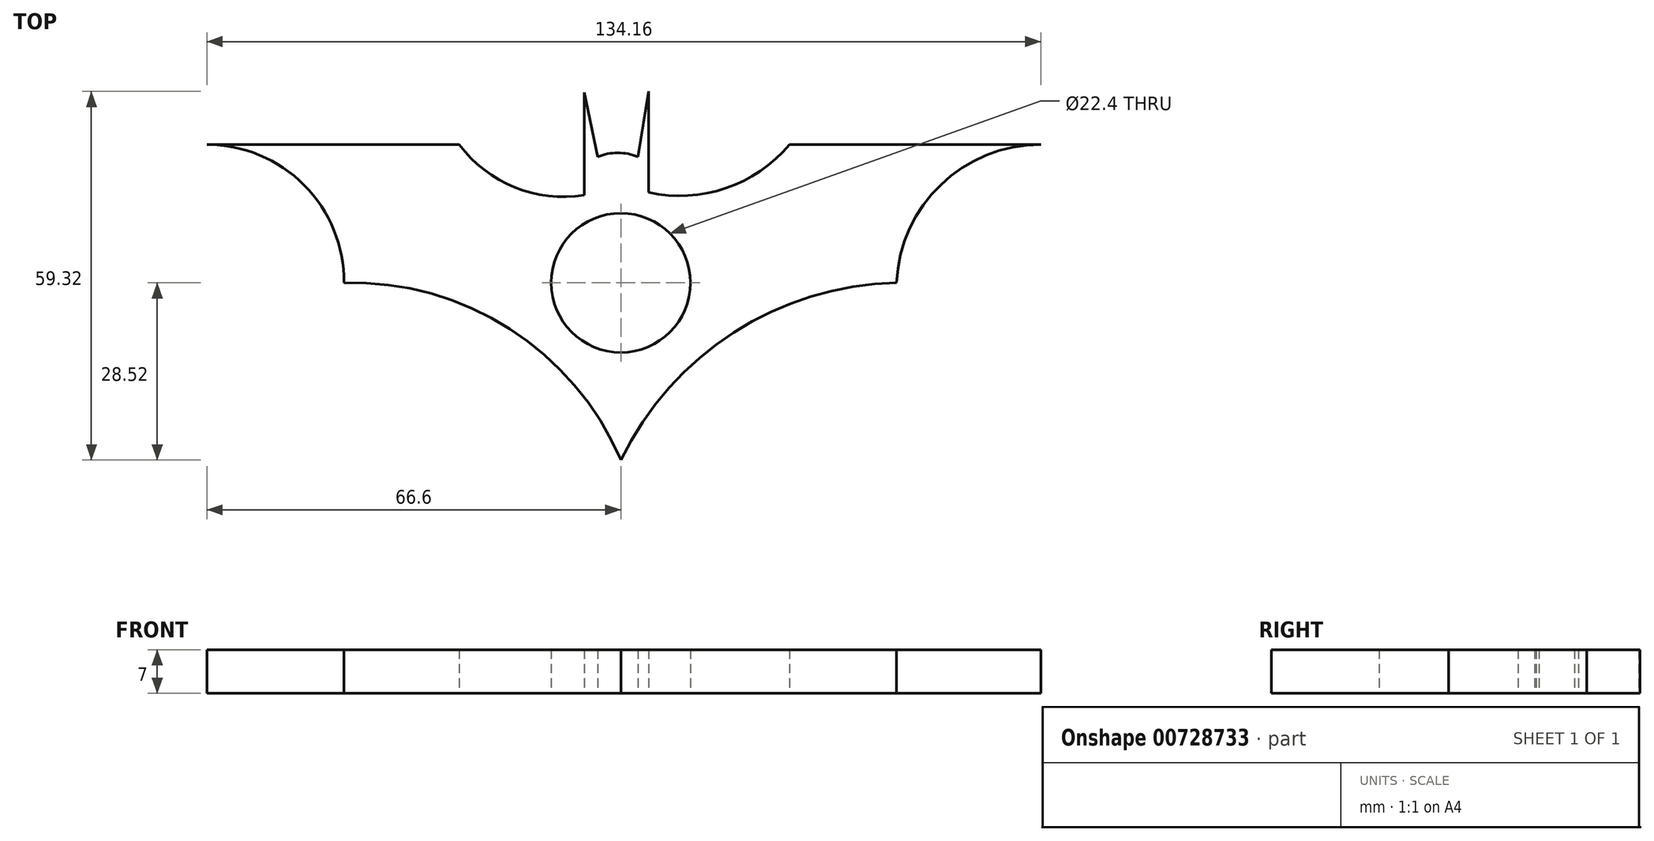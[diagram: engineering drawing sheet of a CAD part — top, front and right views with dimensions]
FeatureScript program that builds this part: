
annotation { "Feature Type Name" : "Feature", "Feature Type Description" : "" }
export const myFeature = defineFeature(function(context is Context, id is Id, definition is map)
    precondition{}
    {
        {
            var Q0;
            Q0=qCreatedBy(makeId("Top.planeOp"),FACE);
            var sketch = newSketch(context, id + "F0", { "sketchPlane" : qUnion([Q0])});
            skLineSegment(sketch, "E0", {"start": v(-66.6, 22.24) * mm, "end": v(-25.99, 22.24) * mm});
            skArc(sketch, "E1", {"start": v(67.56, 22.24) * mm, "mid": v(51.5, 15.78) * mm, "end": v(44.37, 0) * mm});
            skArc(sketch, "E2", {"start": v(-44.55, 0) * mm, "mid": v(-50.94, 15.72) * mm, "end": v(-66.6, 22.24) * mm});
            skArc(sketch, "E3", {"start": v(0, -28.52) * mm, "mid": v(-17.88, -7.4) * mm, "end": v(-44.55, 0) * mm});
            skArc(sketch, "E4", {"start": v(-25.99, 22.24) * mm, "mid": v(-17.09, 15.36) * mm, "end": v(-5.9, 14.12) * mm});
            skLineSegment(sketch, "E5", {"start": v(-5.9, 14.12) * mm, "end": v(-5.9, 30.6) * mm});
            skLineSegment(sketch, "E6", {"start": v(-5.9, 30.6) * mm, "end": v(-3.75, 20.26) * mm});
            skArc(sketch, "E7", {"start": v(2.77, 20.26) * mm, "mid": v(-0.5, 20.9) * mm, "end": v(-3.75, 20.26) * mm});
            skLineSegment(sketch, "E8", {"start": v(2.77, 20.26) * mm, "end": v(4.48, 30.8) * mm});
            skLineSegment(sketch, "E9", {"start": v(4.48, 30.8) * mm, "end": v(4.48, 14.55) * mm});
            skArc(sketch, "E10", {"start": v(4.48, 14.55) * mm, "mid": v(16.89, 15.22) * mm, "end": v(27.15, 22.24) * mm});
            skLineSegment(sketch, "E11.trimOffspring", {"start": v(27.15, 22.24) * mm, "end": v(67.56, 22.24) * mm});
            skArc(sketch, "E12", {"start": v(44.37, 0) * mm, "mid": v(18.16, -8) * mm, "end": v(0, -28.52) * mm});
            skCircle(sketch, "E13", {"center": v(0, 0) * mm, "radius": 11.2 * mm});
            skSolve(sketch);
        }
        {
            var Q0;
            Q0=makeQuery(id+"F0.imprint","IMPRINT",FACE,{"disambiguationData":[TD([[makeQuery(id+"F0.imprint","IMPRINT",EDGE,{"derivedFrom":sQuery(id+"F0.wireOp",EDGE,"E0")}),-1.0]])]});
            extrude(context, id + "F1", {"entities" : qUnion([Q0]), "depth" : 7 * mm, "offsetDistance" : 25 * mm});
        }
    });
